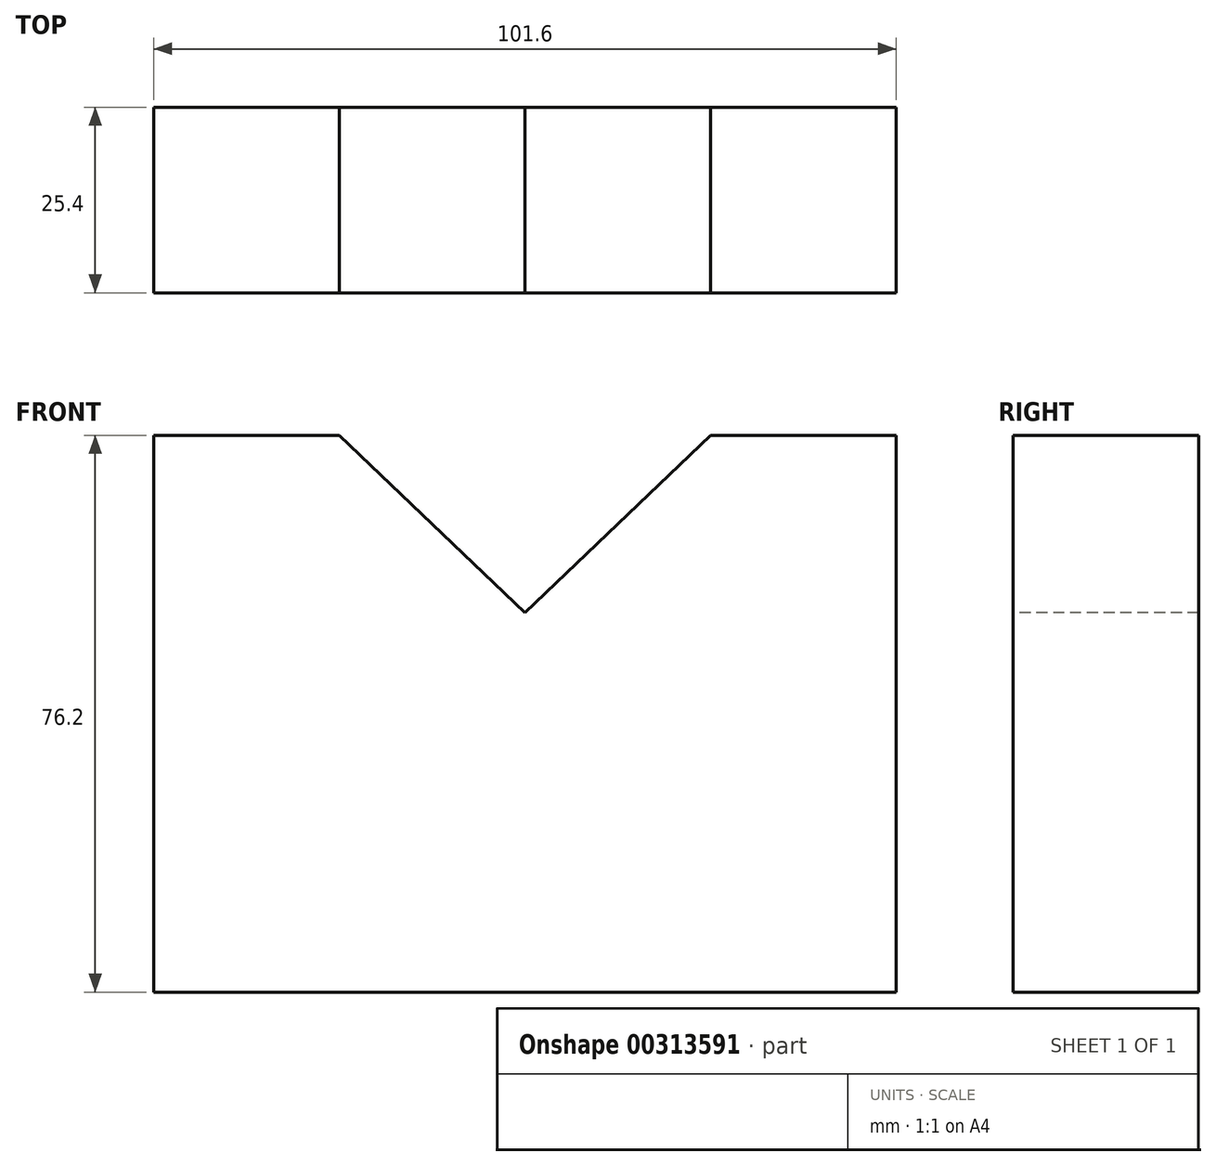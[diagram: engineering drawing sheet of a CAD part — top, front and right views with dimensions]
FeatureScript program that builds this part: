
annotation { "Feature Type Name" : "Feature", "Feature Type Description" : "" }
export const myFeature = defineFeature(function(context is Context, id is Id, definition is map)
    precondition{}
    {
        {
            var Q0;
            Q0=qCreatedBy(makeId("Front.planeOp"),FACE);
            var sketch = newSketch(context, id + "F0", { "sketchPlane" : qUnion([Q0])});
            skLineSegment(sketch, "E0", {"start": v(-47.1, -51.95) * mm, "end": v(54.5, -51.95) * mm});
            skLineSegment(sketch, "E1", {"start": v(54.5, -51.95) * mm, "end": v(54.5, 24.25) * mm});
            skLineSegment(sketch, "E2", {"start": v(54.5, 24.25) * mm, "end": v(29.1, 24.25) * mm});
            skLineSegment(sketch, "E3", {"start": v(-47.1, -51.95) * mm, "end": v(-47.1, 24.25) * mm});
            skLineSegment(sketch, "E4", {"start": v(-47.1, 24.25) * mm, "end": v(-21.7, 24.25) * mm});
            skLineSegment(sketch, "E5", {"start": v(3.7, 0) * mm, "end": v(29.1, 24.25) * mm});
            skLineSegment(sketch, "E6", {"start": v(-21.7, 24.25) * mm, "end": v(3.7, 0) * mm});
            skSolve(sketch);
        }
        {
            var Q0;
            Q0=makeQuery(id+"F0.imprint","IMPRINT",FACE,{"disambiguationData":[TD([[makeQuery(id+"F0.imprint","IMPRINT",EDGE,{"derivedFrom":sQuery(id+"F0.wireOp",EDGE,"E0")}),1.0]])]});
            extrude(context, id + "F1", {"entities" : qUnion([Q0]), "oppositeDirection" : true, "depth" : 25.4 * mm});
        }
    });
